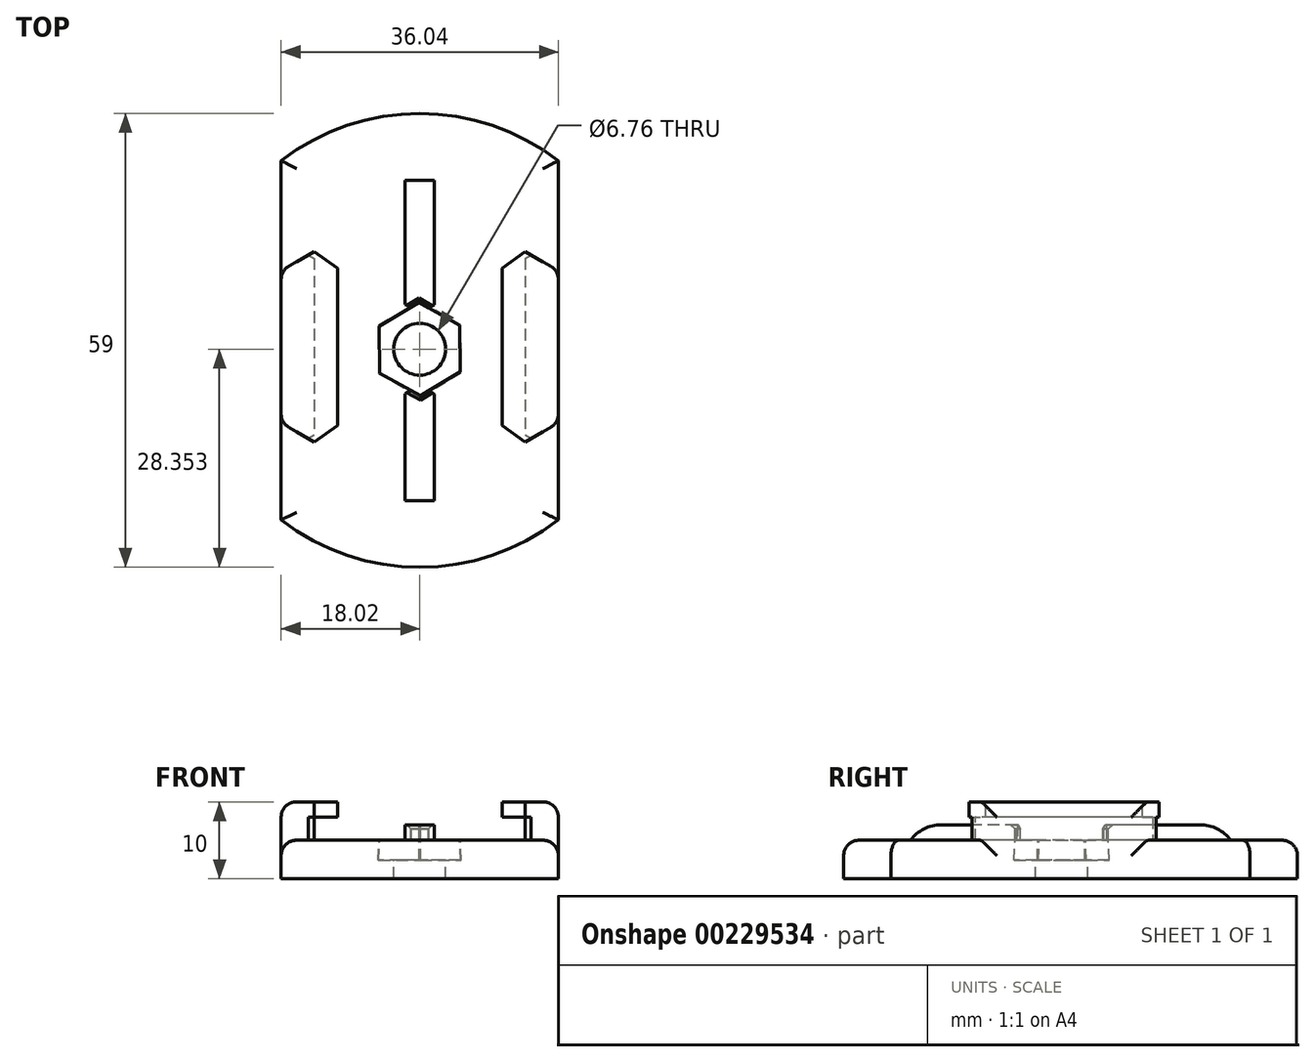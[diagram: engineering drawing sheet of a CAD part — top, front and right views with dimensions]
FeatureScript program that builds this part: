
annotation { "Feature Type Name" : "Feature", "Feature Type Description" : "" }
export const myFeature = defineFeature(function(context is Context, id is Id, definition is map)
    precondition{}
    {
        {
            var Q0;
            Q0=qCreatedBy(makeId("Top.planeOp"),FACE);
            var sketch = newSketch(context, id + "F0", { "sketchPlane" : qUnion([Q0])});
            skArc(sketch, "E0", {"start": v(-18.02, -23.35) * mm, "mid": v(0, -29.5) * mm, "end": v(18.02, -23.35) * mm});
            skLineSegment(sketch, "E1", {"start": v(-18.02, 23.35) * mm, "end": v(-18.02, -23.35) * mm});
            skLineSegment(sketch, "E2.MirrorCS", {"start": v(18.02, 23.35) * mm, "end": v(18.02, -23.35) * mm});
            skArc(sketch, "E3.trimOffspring", {"start": v(18.02, 23.35) * mm, "mid": v(0, 29.5) * mm, "end": v(-18.02, 23.35) * mm});
            skSolve(sketch);
        }
        {
            var Q0;
            Q0 = qSketchRegion(id + "F0", true);
            extrude(context, id + "F1", {"entities" : qUnion([Q0]), "depth" : 5 * mm});
        }
        {
            var Q0;
            Q0=makeQuery(id+"F1.opExtrude","CAP_FACE",FACE,{"disambiguationData":[OSD([sQuery(id+"F0.wireOp",EDGE,"E0"),sQuery(id+"F0.wireOp",EDGE,"E1"),sQuery(id+"F0.wireOp",EDGE,"E2.MirrorCS"),sQuery(id+"F0.wireOp",EDGE,"E3.trimOffspring")])],"isStart":false});
            var sketch = newSketch(context, id + "F2", { "sketchPlane" : qUnion([Q0])});
            skPoint(sketch, "E4", {"position": v(-13.74, 11.54) * mm});
            skPoint(sketch, "E5", {"position": v(-13.74, -13.21) * mm});
            skLineSegment(sketch, "E6", {"start": v(-13.74, 11.54) * mm, "end": v(-18.02, 9.06) * mm});
            skLineSegment(sketch, "E7", {"start": v(-18.02, 9.06) * mm, "end": v(-18.02, -10.74) * mm});
            skLineSegment(sketch, "E8", {"start": v(-18.02, -10.74) * mm, "end": v(-13.74, -13.21) * mm});
            skLineSegment(sketch, "E9", {"start": v(-13.74, 11.54) * mm, "end": v(-13.74, -13.21) * mm});
            skLineSegment(sketch, "E10.MirrorCS", {"start": v(13.74, 11.54) * mm, "end": v(18.02, 9.06) * mm});
            skLineSegment(sketch, "E11.MirrorCS", {"start": v(13.74, 11.54) * mm, "end": v(13.74, -13.21) * mm});
            skLineSegment(sketch, "E12.MirrorCS", {"start": v(18.02, -10.74) * mm, "end": v(13.74, -13.21) * mm});
            skLineSegment(sketch, "E13.MirrorCS", {"start": v(18.02, 9.06) * mm, "end": v(18.02, -10.74) * mm});
            skSolve(sketch);
        }
        {
            var Q0;
            Q0=makeQuery(id+"F2.imprint","IMPRINT",FACE,{"disambiguationData":[TD([[makeQuery(id+"F2.imprint","IMPRINT",EDGE,{"derivedFrom":sQuery(id+"F2.wireOp",EDGE,"E6")}),1.0]])]});
            var Q1;
            Q1=makeQuery(id+"F2.imprint","IMPRINT",FACE,{"disambiguationData":[TD([[makeQuery(id+"F2.imprint","IMPRINT",EDGE,{"derivedFrom":sQuery(id+"F2.wireOp",EDGE,"E10.MirrorCS")}),-1.0]])]});
            extrude(context, id + "F3", {"entities" : qUnion([Q0, Q1]), "operationType" : NewBodyOperationType.ADD, "depth" : 5 * mm});
        }
        {
            var Q0;
            Q0=makeQuery(id+"F3.opExtrude","CAP_FACE",FACE,{"disambiguationData":[OSD([sQuery(id+"F2.wireOp",EDGE,"E6"),sQuery(id+"F2.wireOp",EDGE,"E7"),sQuery(id+"F2.wireOp",EDGE,"E8"),sQuery(id+"F2.wireOp",EDGE,"E9")])],"isStart":false});
            var sketch = newSketch(context, id + "F4", { "sketchPlane" : qUnion([Q0])});
            skPoint(sketch, "E14", {"position": v(-18.02, -0.84) * mm});
            skLineSegment(sketch, "E15", {"start": v(-10.7, 9.38) * mm, "end": v(-10.7, -11.05) * mm});
            skPoint(sketch, "E16", {"position": v(-10.7, -0.84) * mm});
            skLineSegment(sketch, "E17", {"start": v(-10.7, 9.38) * mm, "end": v(-13.74, 11.54) * mm});
            skLineSegment(sketch, "E18", {"start": v(-13.74, 11.54) * mm, "end": v(-13.74, -13.21) * mm});
            skLineSegment(sketch, "E19", {"start": v(-13.74, -13.21) * mm, "end": v(-10.7, -11.05) * mm});
            skLineSegment(sketch, "E20.MirrorCS", {"start": v(10.7, 9.38) * mm, "end": v(13.74, 11.54) * mm});
            skLineSegment(sketch, "E21.MirrorCS", {"start": v(10.7, 9.38) * mm, "end": v(10.7, -11.05) * mm});
            skLineSegment(sketch, "E22.MirrorCS", {"start": v(13.74, -13.21) * mm, "end": v(10.7, -11.05) * mm});
            skLineSegment(sketch, "E23.MirrorCS", {"start": v(13.74, 11.54) * mm, "end": v(13.74, -13.21) * mm});
            skSolve(sketch);
        }
        {
            var Q0;
            Q0 = qSketchRegion(id + "F4", true);
            extrude(context, id + "F5", {"entities" : qUnion([Q0]), "operationType" : NewBodyOperationType.ADD, "oppositeDirection" : true, "depth" : 2 * mm});
        }
        {
            var Q0;
            Q0=makeQuery(id+"F1.opExtrude","CAP_FACE",FACE,{"disambiguationData":[OSD([sQuery(id+"F0.wireOp",EDGE,"E0"),sQuery(id+"F0.wireOp",EDGE,"E1"),sQuery(id+"F0.wireOp",EDGE,"E2.MirrorCS"),sQuery(id+"F0.wireOp",EDGE,"E3.trimOffspring")])],"isStart":false});
            var sketch = newSketch(context, id + "F6", { "sketchPlane" : qUnion([Q0])});
            skLineSegment(sketch, "E24.bottom", {"start": v(1.9, 20.83) * mm, "end": v(-1.9, 20.83) * mm});
            skLineSegment(sketch, "E24.top", {"start": v(1.9, -20.83) * mm, "end": v(-1.9, -20.83) * mm});
            skLineSegment(sketch, "E24.left", {"start": v(1.9, 20.83) * mm, "end": v(1.9, -20.83) * mm});
            skLineSegment(sketch, "E24.right", {"start": v(-1.9, 20.83) * mm, "end": v(-1.9, -20.83) * mm});
            skPoint(sketch, "E24.middle", {"position": v(0, 0) * mm});
            skSolve(sketch);
        }
        {
            var Q0;
            Q0=makeQuery(id+"F6.imprint","IMPRINT",FACE,{"disambiguationData":[TD([[makeQuery(id+"F6.imprint","IMPRINT",EDGE,{"derivedFrom":sQuery(id+"F6.wireOp",EDGE,"E24.bottom")}),1.0]])]});
            extrude(context, id + "F7", {"entities" : qUnion([Q0]), "operationType" : NewBodyOperationType.ADD, "depth" : 2 * mm});
        }
        {
            var Q0;
            Q0=makeQuery(id+"F7.opExtrude","CAP_EDGE",EDGE,{"disambiguationData":[OSD([sQuery(id+"F6.wireOp",EDGE,"E24.bottom")])],"isStart":false});
            var Q1;
            Q1=makeQuery(id+"F7.opExtrude","CAP_EDGE",EDGE,{"disambiguationData":[OSD([sQuery(id+"F6.wireOp",EDGE,"E24.top")])],"isStart":false});
            fillet(context, id + "F8", {"entities" : qUnion([Q0, Q1]), "radius" : 5 * mm, "tangentPropagation" : true, "allowEdgeOverflow" : false});
        }
        {
            var Q0;
            Q0=makeQuery(id+"F1.opExtrude","CAP_FACE",FACE,{"disambiguationData":[OSD([sQuery(id+"F0.wireOp",EDGE,"E0"),sQuery(id+"F0.wireOp",EDGE,"E1"),sQuery(id+"F0.wireOp",EDGE,"E2.MirrorCS"),sQuery(id+"F0.wireOp",EDGE,"E3.trimOffspring")])],"isStart":false});
            var sketch = newSketch(context, id + "F9", { "sketchPlane" : qUnion([Q0])});
            skCircle(sketch, "E25.cCircle", {"center": v(0, -1.15) * mm, "radius": 5.24 * mm, "construction": true});
            skLineSegment(sketch, "E25.0", {"start": v(-0.1, 4.9) * mm, "end": v(5.2, 1.96) * mm});
            skLineSegment(sketch, "E25.1", {"start": v(5.2, 1.96) * mm, "end": v(5.28, -4.1) * mm});
            skLineSegment(sketch, "E25.2", {"start": v(5.28, -4.1) * mm, "end": v(0.1, -7.2) * mm});
            skLineSegment(sketch, "E25.3", {"start": v(0.1, -7.2) * mm, "end": v(-5.2, -4.25) * mm});
            skLineSegment(sketch, "E25.4", {"start": v(-5.2, -4.25) * mm, "end": v(-5.28, 1.8) * mm});
            skLineSegment(sketch, "E25.5", {"start": v(-5.28, 1.8) * mm, "end": v(-0.1, 4.9) * mm});
            skPoint(sketch, "E25.0.midPoint", {"position": v(2.55, 3.43) * mm});
            skSolve(sketch);
        }
        {
            var Q0;
            Q0 = qSketchRegion(id + "F9", true);
            extrude(context, id + "F10", {"entities" : qUnion([Q0]), "operationType" : NewBodyOperationType.REMOVE, "oppositeDirection" : true, "depth" : 2.6 * mm, "hasDraft" : true, "draftAngle" : 3 * degree, "hasSecondDirection" : true, "secondDirectionOppositeDirection" : false, "secondDirectionDepth" : 25 * mm});
        }
        {
            var Q0;
            Q0=sQuery(id+"F9.wireOp",VERTEX,"E25.cCircle.center");
            var Q1;
            Q1=makeQuery(id+"F1.opExtrude","SWEPT_BODY",BODY,{"disambiguationData":[OSD([sQuery(id+"F0.wireOp",EDGE,"E0"),sQuery(id+"F0.wireOp",EDGE,"E1"),sQuery(id+"F0.wireOp",EDGE,"E2.MirrorCS"),sQuery(id+"F0.wireOp",EDGE,"E3.trimOffspring")])]});
            hole(context, id + "F11", {"style" : HoleStyle.SIMPLE, "endStyle" : HoleEndStyle.THROUGH, "standardTappedOrClearance" : lookupTablePath({ "standard" : "ANSI", "fit" : "Normal (ASME)", "size" : "1/4", "type" : "Clearance" }), "standardBlindInLast" : lookupTablePath({ "fit" : "Free", "standard" : "ANSI", "size" : "1/4", "type" : "Clearance" }), "holeDiameter" : 6.76 * mm, "tappedDepth" : 12 * mm, "tapClearance" : 3, "locations" : qUnion([Q0]), "scope" : qUnion([Q1])});
        }
        {
            var Q0;
            Q0=makeQuery(id+"F5.boolean.opBoolean","SPLIT",EDGE,{"derivedFrom":makeQuery(id+"F3.opExtrude","SWEPT_EDGE",EDGE,{"disambiguationData":[OSD([sQuery(id+"F2.wireOp",EDGE,"E8"),sQuery(id+"F2.wireOp",EDGE,"E9")])]})});
            var Q1;
            Q1=makeQuery(id+"F5.boolean.opBoolean","SPLIT",EDGE,{"derivedFrom":makeQuery(id+"F3.opExtrude","SWEPT_EDGE",EDGE,{"disambiguationData":[OSD([sQuery(id+"F2.wireOp",EDGE,"E11.MirrorCS"),sQuery(id+"F2.wireOp",EDGE,"E12.MirrorCS")])]})});
            var Q2;
            Q2=makeQuery(id+"F5.boolean.opBoolean","SPLIT",EDGE,{"derivedFrom":makeQuery(id+"F3.opExtrude","SWEPT_EDGE",EDGE,{"disambiguationData":[OSD([sQuery(id+"F2.wireOp",EDGE,"E6"),sQuery(id+"F2.wireOp",EDGE,"E9")])]})});
            var Q3;
            Q3=makeQuery(id+"F5.boolean.opBoolean","SPLIT",EDGE,{"derivedFrom":makeQuery(id+"F3.opExtrude","SWEPT_EDGE",EDGE,{"disambiguationData":[OSD([sQuery(id+"F2.wireOp",EDGE,"E10.MirrorCS"),sQuery(id+"F2.wireOp",EDGE,"E11.MirrorCS")])]})});
            var Q4;
            Q4=makeQuery(id+"F10.boolean.opBoolean","INTERSECT",EDGE,{"derivedFrom":[makeQuery(id+"F7.opExtrude","SWEPT_FACE",FACE,{"disambiguationData":[OSD([sQuery(id+"F6.wireOp",EDGE,"E24.left")])]}),makeQuery(id+"F10.*.split.splitOp","SPLIT",FACE,{"derivedFrom":makeQuery(id+"F10.opExtrude","SWEPT_FACE",FACE,{"disambiguationData":[OSD([sQuery(id+"F9.wireOp",EDGE,"E25.0")])]}),"isFromBackBody":true})]});
            var Q5;
            Q5=makeQuery(id+"F10.boolean.opBoolean","INTERSECT",EDGE,{"derivedFrom":[makeQuery(id+"F7.opExtrude","SWEPT_FACE",FACE,{"disambiguationData":[OSD([sQuery(id+"F6.wireOp",EDGE,"E24.right")])]}),makeQuery(id+"F10.*.split.splitOp","SPLIT",FACE,{"derivedFrom":makeQuery(id+"F10.opExtrude","SWEPT_FACE",FACE,{"disambiguationData":[OSD([sQuery(id+"F9.wireOp",EDGE,"E25.5")])]}),"isFromBackBody":true})]});
            var Q6;
            Q6=makeQuery(id+"F10.boolean.opBoolean","INTERSECT",EDGE,{"derivedFrom":[makeQuery(id+"F7.opExtrude","CAP_FACE",FACE,{"disambiguationData":[OSD([sQuery(id+"F6.wireOp",EDGE,"E24.bottom"),sQuery(id+"F6.wireOp",EDGE,"E24.top"),sQuery(id+"F6.wireOp",EDGE,"E24.left"),sQuery(id+"F6.wireOp",EDGE,"E24.right")])],"isStart":false}),makeQuery(id+"F10.*.split.splitOp","SPLIT",FACE,{"derivedFrom":makeQuery(id+"F10.opExtrude","SWEPT_FACE",FACE,{"disambiguationData":[OSD([sQuery(id+"F9.wireOp",EDGE,"E25.5")])]}),"isFromBackBody":true})]});
            var Q7;
            Q7=makeQuery(id+"F10.boolean.opBoolean","INTERSECT",EDGE,{"derivedFrom":[makeQuery(id+"F7.opExtrude","CAP_FACE",FACE,{"disambiguationData":[OSD([sQuery(id+"F6.wireOp",EDGE,"E24.bottom"),sQuery(id+"F6.wireOp",EDGE,"E24.top"),sQuery(id+"F6.wireOp",EDGE,"E24.left"),sQuery(id+"F6.wireOp",EDGE,"E24.right")])],"isStart":false}),makeQuery(id+"F10.*.split.splitOp","SPLIT",FACE,{"derivedFrom":makeQuery(id+"F10.opExtrude","SWEPT_FACE",FACE,{"disambiguationData":[OSD([sQuery(id+"F9.wireOp",EDGE,"E25.0")])]}),"isFromBackBody":true})]});
            var Q8;
            Q8=makeQuery(id+"F10.boolean.opBoolean","INTERSECT",EDGE,{"derivedFrom":[makeQuery(id+"F7.opExtrude","CAP_FACE",FACE,{"disambiguationData":[OSD([sQuery(id+"F6.wireOp",EDGE,"E24.bottom"),sQuery(id+"F6.wireOp",EDGE,"E24.top"),sQuery(id+"F6.wireOp",EDGE,"E24.left"),sQuery(id+"F6.wireOp",EDGE,"E24.right")])],"isStart":false}),makeQuery(id+"F10.*.split.splitOp","SPLIT",FACE,{"derivedFrom":makeQuery(id+"F10.opExtrude","SWEPT_FACE",FACE,{"disambiguationData":[OSD([sQuery(id+"F9.wireOp",EDGE,"E25.3")])]}),"isFromBackBody":true})]});
            var Q9;
            Q9=makeQuery(id+"F10.boolean.opBoolean","INTERSECT",EDGE,{"derivedFrom":[makeQuery(id+"F7.opExtrude","CAP_FACE",FACE,{"disambiguationData":[OSD([sQuery(id+"F6.wireOp",EDGE,"E24.bottom"),sQuery(id+"F6.wireOp",EDGE,"E24.top"),sQuery(id+"F6.wireOp",EDGE,"E24.left"),sQuery(id+"F6.wireOp",EDGE,"E24.right")])],"isStart":false}),makeQuery(id+"F10.*.split.splitOp","SPLIT",FACE,{"derivedFrom":makeQuery(id+"F10.opExtrude","SWEPT_FACE",FACE,{"disambiguationData":[OSD([sQuery(id+"F9.wireOp",EDGE,"E25.2")])]}),"isFromBackBody":true})]});
            var Q10;
            Q10=makeQuery(id+"F10.boolean.opBoolean","INTERSECT",EDGE,{"derivedFrom":[makeQuery(id+"F7.opExtrude","SWEPT_FACE",FACE,{"disambiguationData":[OSD([sQuery(id+"F6.wireOp",EDGE,"E24.left")])]}),makeQuery(id+"F10.*.split.splitOp","SPLIT",FACE,{"derivedFrom":makeQuery(id+"F10.opExtrude","SWEPT_FACE",FACE,{"disambiguationData":[OSD([sQuery(id+"F9.wireOp",EDGE,"E25.2")])]}),"isFromBackBody":true})]});
            var Q11;
            Q11=makeQuery(id+"F10.boolean.opBoolean","INTERSECT",EDGE,{"derivedFrom":[makeQuery(id+"F7.opExtrude","SWEPT_FACE",FACE,{"disambiguationData":[OSD([sQuery(id+"F6.wireOp",EDGE,"E24.right")])]}),makeQuery(id+"F10.*.split.splitOp","SPLIT",FACE,{"derivedFrom":makeQuery(id+"F10.opExtrude","SWEPT_FACE",FACE,{"disambiguationData":[OSD([sQuery(id+"F9.wireOp",EDGE,"E25.3")])]}),"isFromBackBody":true})]});
            chamfer(context, id + "F12", {"entities" : qUnion([Q0, Q1, Q2, Q3, Q4, Q5, Q6, Q7, Q8, Q9, Q10, Q11]), "width" : .5 * mm});
        }
        {
            var Q0;
            Q0=makeQuery(id+"F3.opExtrude","CAP_EDGE",EDGE,{"disambiguationData":[OSD([sQuery(id+"F2.wireOp",EDGE,"E7")])],"isStart":false});
            var Q1;
            Q1=makeQuery(id+"F3.opExtrude","CAP_EDGE",EDGE,{"disambiguationData":[OSD([sQuery(id+"F2.wireOp",EDGE,"E13.MirrorCS")])],"isStart":false});
            var Q2;
            Q2=makeQuery(id+"F3.opExtrude","SWEPT_EDGE",EDGE,{"disambiguationData":[OSD([sQuery(id+"F0.wireOp",EDGE,"E2.MirrorCS"),sQuery(id+"F2.wireOp",EDGE,"E12.MirrorCS"),sQuery(id+"F2.wireOp",EDGE,"E13.MirrorCS")])]});
            var Q3;
            Q3=makeQuery(id+"F3.opExtrude","SWEPT_EDGE",EDGE,{"disambiguationData":[OSD([sQuery(id+"F0.wireOp",EDGE,"E1"),sQuery(id+"F2.wireOp",EDGE,"E7"),sQuery(id+"F2.wireOp",EDGE,"E8")])]});
            var Q4;
            Q4=makeQuery(id+"F3.opExtrude","SWEPT_EDGE",EDGE,{"disambiguationData":[OSD([sQuery(id+"F0.wireOp",EDGE,"E1"),sQuery(id+"F2.wireOp",EDGE,"E6"),sQuery(id+"F2.wireOp",EDGE,"E7")])]});
            var Q5;
            Q5=makeQuery(id+"F3.opExtrude","SWEPT_EDGE",EDGE,{"disambiguationData":[OSD([sQuery(id+"F0.wireOp",EDGE,"E2.MirrorCS"),sQuery(id+"F2.wireOp",EDGE,"E10.MirrorCS"),sQuery(id+"F2.wireOp",EDGE,"E13.MirrorCS")])]});
            var Q6;
            {var subQ0=sQuery(id+"F0.wireOp",EDGE,"E3.trimOffspring");var subQ1=sQuery(id+"F0.wireOp",EDGE,"E2.MirrorCS");Q6=makeQuery(id+"F3.boolean.opBoolean","SPLIT",EDGE,{"disambiguationData":[TD([makeQuery(id+"F1.opExtrude","SWEPT_FACE",FACE,{"disambiguationData":[OSD([subQ0])]})])],"derivedFrom":makeQuery(id+"F1.opExtrude","CAP_EDGE",EDGE,{"disambiguationData":[OSD([subQ1])],"isStart":false})});}
            var Q7;
            Q7=makeQuery(id+"F1.opExtrude","CAP_EDGE",EDGE,{"disambiguationData":[OSD([sQuery(id+"F0.wireOp",EDGE,"E3.trimOffspring")])],"isStart":false});
            var Q8;
            {var subQ0=sQuery(id+"F0.wireOp",EDGE,"E3.trimOffspring");var subQ1=sQuery(id+"F0.wireOp",EDGE,"E1");Q8=makeQuery(id+"F3.boolean.opBoolean","SPLIT",EDGE,{"disambiguationData":[TD([makeQuery(id+"F1.opExtrude","SWEPT_FACE",FACE,{"disambiguationData":[OSD([subQ0])]})])],"derivedFrom":makeQuery(id+"F1.opExtrude","CAP_EDGE",EDGE,{"disambiguationData":[OSD([subQ1])],"isStart":false})});}
            var Q9;
            {var subQ0=sQuery(id+"F0.wireOp",EDGE,"E0");var subQ1=sQuery(id+"F0.wireOp",EDGE,"E2.MirrorCS");Q9=makeQuery(id+"F3.boolean.opBoolean","SPLIT",EDGE,{"disambiguationData":[TD([makeQuery(id+"F1.opExtrude","SWEPT_FACE",FACE,{"disambiguationData":[OSD([subQ0])]})])],"derivedFrom":makeQuery(id+"F1.opExtrude","CAP_EDGE",EDGE,{"disambiguationData":[OSD([subQ1])],"isStart":false})});}
            var Q10;
            Q10=makeQuery(id+"F1.opExtrude","CAP_EDGE",EDGE,{"disambiguationData":[OSD([sQuery(id+"F0.wireOp",EDGE,"E0")])],"isStart":false});
            var Q11;
            {var subQ0=sQuery(id+"F0.wireOp",EDGE,"E1");var subQ1=sQuery(id+"F0.wireOp",EDGE,"E0");Q11=makeQuery(id+"F3.boolean.opBoolean","SPLIT",EDGE,{"disambiguationData":[TD([makeQuery(id+"F1.opExtrude","SWEPT_FACE",FACE,{"disambiguationData":[OSD([subQ1])]})])],"derivedFrom":makeQuery(id+"F1.opExtrude","CAP_EDGE",EDGE,{"disambiguationData":[OSD([subQ0])],"isStart":false})});}
            fillet(context, id + "F13", {"entities" : qUnion([Q0, Q1, Q2, Q3, Q4, Q5, Q6, Q7, Q8, Q9, Q10, Q11]), "radius" : 2 * mm, "tangentPropagation" : true, "allowEdgeOverflow" : false});
        }
    });
